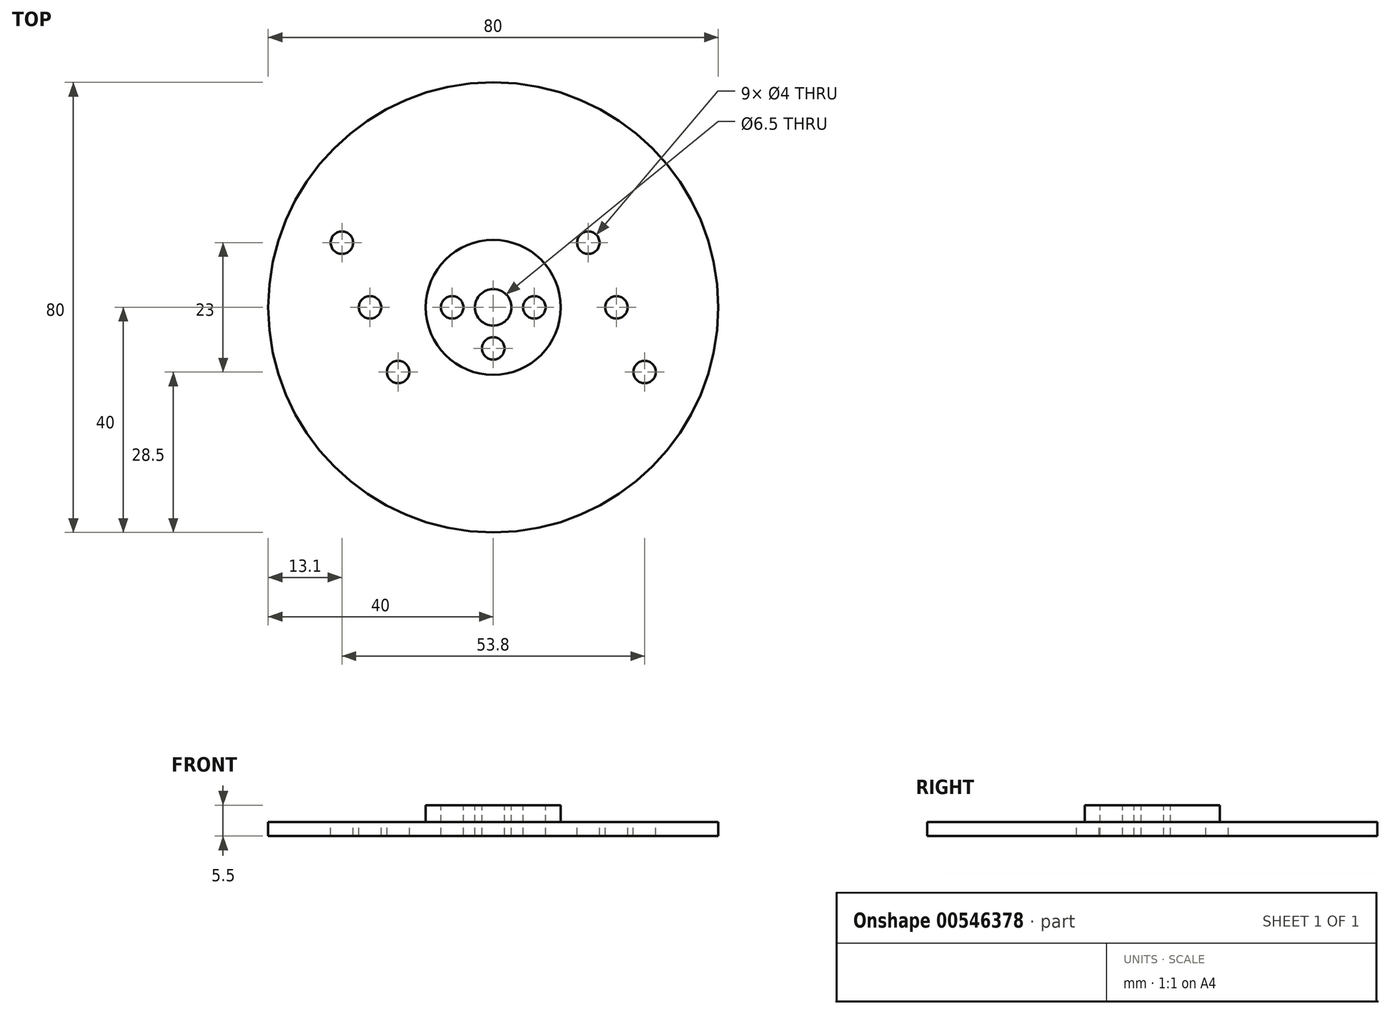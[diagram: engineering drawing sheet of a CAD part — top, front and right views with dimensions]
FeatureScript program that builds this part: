
annotation { "Feature Type Name" : "Feature", "Feature Type Description" : "" }
export const myFeature = defineFeature(function(context is Context, id is Id, definition is map)
    precondition{}
    {
        {
            var Q0;
            Q0=qCreatedBy(makeId("Top.planeOp"),FACE);
            var sketch = newSketch(context, id + "F0", { "sketchPlane" : qUnion([Q0])});
            skCircle(sketch, "E0", {"center": v(0, 0) * mm, "radius": 40 * mm});
            skSolve(sketch);
        }
        {
            var Q0;
            Q0=makeQuery(id+"F0.imprint","IMPRINT",FACE,{"disambiguationData":[TD([[makeQuery(id+"F0.imprint","IMPRINT",EDGE,{"derivedFrom":sQuery(id+"F0.wireOp",EDGE,"E0")}),1.0]])]});
            extrude(context, id + "F1", {"entities" : qUnion([Q0]), "depth" : 2.5 * mm, "offsetDistance" : 25 * mm});
        }
        {
            var Q0;
            Q0=makeQuery(id+"F1.opExtrude","CAP_FACE",FACE,{"disambiguationData":[OSD([sQuery(id+"F0.wireOp",EDGE,"E0")])],"isStart":false});
            var sketch = newSketch(context, id + "F2", { "sketchPlane" : qUnion([Q0])});
            skCircle(sketch, "E1", {"center": v(0, 0) * mm, "radius": 12 * mm});
            skSolve(sketch);
        }
        {
            var Q0;
            Q0=makeQuery(id+"F2.imprint","IMPRINT",FACE,{"disambiguationData":[TD([[makeQuery(id+"F2.imprint","IMPRINT",EDGE,{"derivedFrom":sQuery(id+"F2.wireOp",EDGE,"E1")}),1.0]])]});
            var Q1;
            Q1=sQuery(id+"F2.wireOp",EDGE,"E1");
            extrude(context, id + "F3", {"entities" : qUnion([Q0]), "operationType" : NewBodyOperationType.ADD, "surfaceEntities" : qUnion([Q1]), "depth" : 3 * mm, "offsetDistance" : 25 * mm});
        }
        {
            var Q0;
            Q0=makeQuery(id+"F3.opExtrude","CAP_FACE",FACE,{"disambiguationData":[OSD([sQuery(id+"F2.wireOp",EDGE,"E1")])],"isStart":false});
            var sketch = newSketch(context, id + "F4", { "sketchPlane" : qUnion([Q0])});
            skLineSegment(sketch, "E2", {"start": v(0, 0) * mm, "end": v(7.3, 0) * mm, "construction": true});
            skLineSegment(sketch, "E3.MirrorCS", {"start": v(0, 0) * mm, "end": v(-7.3, 0) * mm, "construction": true});
            skLineSegment(sketch, "E4", {"start": v(0, 0) * mm, "end": v(0, -7.3) * mm, "construction": true});
            skCircle(sketch, "E5", {"center": v(-7.3, 0) * mm, "radius": 2 * mm});
            skCircle(sketch, "E6", {"center": v(7.3, 0) * mm, "radius": 2 * mm});
            skCircle(sketch, "E7", {"center": v(0, -7.3) * mm, "radius": 2 * mm});
            skSolve(sketch);
        }
        {
            var Q0;
            Q0 = qSketchRegion(id + "F4", true);
            extrude(context, id + "F5", {"entities" : qUnion([Q0]), "operationType" : NewBodyOperationType.REMOVE, "oppositeDirection" : true, "depth" : 25 * mm, "offsetDistance" : 25 * mm});
        }
        {
            var Q0;
            Q0=makeQuery(id+"F3.opExtrude","CAP_FACE",FACE,{"disambiguationData":[OSD([sQuery(id+"F2.wireOp",EDGE,"E1")])],"isStart":false});
            var sketch = newSketch(context, id + "F6", { "sketchPlane" : qUnion([Q0])});
            skCircle(sketch, "E8", {"center": v(0, 0) * mm, "radius": 3.25 * mm});
            skSolve(sketch);
        }
        {
            var Q0;
            Q0=makeQuery(id+"F6.imprint","IMPRINT",FACE,{"disambiguationData":[TD([[makeQuery(id+"F6.imprint","IMPRINT",EDGE,{"derivedFrom":sQuery(id+"F6.wireOp",EDGE,"E8")}),1.0]])]});
            var Q1;
            Q1=sQuery(id+"F6.wireOp",EDGE,"E8");
            extrude(context, id + "F7", {"entities" : qUnion([Q0]), "operationType" : NewBodyOperationType.REMOVE, "surfaceEntities" : qUnion([Q1]), "oppositeDirection" : true, "depth" : 25 * mm, "offsetDistance" : 25 * mm});
        }
        {
            var Q0;
            Q0=makeQuery(id+"F1.opExtrude","CAP_FACE",FACE,{"disambiguationData":[OSD([sQuery(id+"F0.wireOp",EDGE,"E0")])],"isStart":false});
            var sketch = newSketch(context, id + "F8", { "sketchPlane" : qUnion([Q0])});
            skSolve(sketch);
        }
        {
            var Q0;
            Q0=makeQuery(id+"F8.imprint","IMPRINT",FACE,{"disambiguationData":[TD([[makeQuery(id+"F8.imprint","IMPRINT",EDGE,{"derivedFrom":makeQuery(id+"F1.opExtrude","CAP_EDGE",EDGE,{"disambiguationData":[OSD([sQuery(id+"F0.wireOp",EDGE,"E0")])],"isStart":false})}),1.0]])]});
            var sketch = newSketch(context, id + "F9", { "sketchPlane" : qUnion([Q0])});
            skLineSegment(sketch, "E9", {"start": v(0, 0) * mm, "end": v(-7.3, 0) * mm, "construction": true});
            skLineSegment(sketch, "E10", {"start": v(-7.3, 0) * mm, "end": v(-16.9, 0) * mm, "construction": true});
            skLineSegment(sketch, "E11", {"start": v(-16.9, 0) * mm, "end": v(-21.9, 0) * mm, "construction": true});
            skLineSegment(sketch, "E12", {"start": v(-21.9, 0) * mm, "end": v(-26.9, 0) * mm, "construction": true});
            skLineSegment(sketch, "E13", {"start": v(-26.9, 0) * mm, "end": v(-39.9, 0) * mm, "construction": true});
            skLineSegment(sketch, "E14", {"start": v(0, 0) * mm, "end": v(0, 11.5) * mm, "construction": true});
            skLineSegment(sketch, "E15", {"start": v(0, 0) * mm, "end": v(0, -11.5) * mm, "construction": true});
            skCircle(sketch, "E16", {"center": v(-26.9, 11.5) * mm, "radius": 2 * mm});
            skCircle(sketch, "E17", {"center": v(-21.9, 0) * mm, "radius": 2 * mm});
            skCircle(sketch, "E18", {"center": v(-16.9, -11.5) * mm, "radius": 2 * mm});
            skLineSegment(sketch, "E19.MirrorCS", {"start": v(26.9, 0) * mm, "end": v(39.9, 0) * mm, "construction": true});
            skLineSegment(sketch, "E20.MirrorCS", {"start": v(21.9, 0) * mm, "end": v(26.9, 0) * mm, "construction": true});
            skLineSegment(sketch, "E21.MirrorCS", {"start": v(16.9, 0) * mm, "end": v(21.9, 0) * mm, "construction": true});
            skLineSegment(sketch, "E22.MirrorCS", {"start": v(0, 0) * mm, "end": v(7.3, 0) * mm, "construction": true});
            skLineSegment(sketch, "E23.MirrorCS", {"start": v(7.3, 0) * mm, "end": v(16.9, 0) * mm, "construction": true});
            skCircle(sketch, "E24", {"center": v(16.9, 11.5) * mm, "radius": 2 * mm});
            skCircle(sketch, "E25", {"center": v(21.9, 0) * mm, "radius": 2 * mm});
            skCircle(sketch, "E26", {"center": v(26.9, -11.5) * mm, "radius": 2 * mm});
            skSolve(sketch);
        }
        {
            var Q0;
            Q0=makeQuery(id+"F9.imprint","IMPRINT",FACE,{"disambiguationData":[TD([[makeQuery(id+"F9.imprint","IMPRINT",EDGE,{"derivedFrom":sQuery(id+"F9.wireOp",EDGE,"E25")}),1.0]])]});
            var Q1;
            Q1=makeQuery(id+"F9.imprint","IMPRINT",FACE,{"disambiguationData":[TD([[makeQuery(id+"F9.imprint","IMPRINT",EDGE,{"derivedFrom":sQuery(id+"F9.wireOp",EDGE,"E24")}),1.0]])]});
            var Q2;
            Q2=makeQuery(id+"F9.imprint","IMPRINT",FACE,{"disambiguationData":[TD([[makeQuery(id+"F9.imprint","IMPRINT",EDGE,{"derivedFrom":sQuery(id+"F9.wireOp",EDGE,"E26")}),1.0]])]});
            var Q3;
            Q3=makeQuery(id+"F9.imprint","IMPRINT",FACE,{"disambiguationData":[TD([[makeQuery(id+"F9.imprint","IMPRINT",EDGE,{"derivedFrom":sQuery(id+"F9.wireOp",EDGE,"E16")}),1.0]])]});
            var Q4;
            Q4=makeQuery(id+"F9.imprint","IMPRINT",FACE,{"disambiguationData":[TD([[makeQuery(id+"F9.imprint","IMPRINT",EDGE,{"derivedFrom":sQuery(id+"F9.wireOp",EDGE,"E17")}),1.0]])]});
            var Q5;
            Q5=makeQuery(id+"F9.imprint","IMPRINT",FACE,{"disambiguationData":[TD([[makeQuery(id+"F9.imprint","IMPRINT",EDGE,{"derivedFrom":sQuery(id+"F9.wireOp",EDGE,"E18")}),1.0]])]});
            var Q6;
            Q6=sQuery(id+"F9.wireOp",EDGE,"E16");
            var Q7;
            Q7=sQuery(id+"F9.wireOp",EDGE,"E17");
            var Q8;
            Q8=sQuery(id+"F9.wireOp",EDGE,"E18");
            var Q9;
            Q9=sQuery(id+"F9.wireOp",EDGE,"E24");
            var Q10;
            Q10=sQuery(id+"F9.wireOp",EDGE,"E25");
            var Q11;
            Q11=sQuery(id+"F9.wireOp",EDGE,"E26");
            extrude(context, id + "F10", {"entities" : qUnion([Q0, Q1, Q2, Q3, Q4, Q5]), "operationType" : NewBodyOperationType.REMOVE, "surfaceEntities" : qUnion([Q6, Q7, Q8, Q9, Q10, Q11]), "oppositeDirection" : true, "depth" : 25 * mm, "offsetDistance" : 25 * mm});
        }
    });
